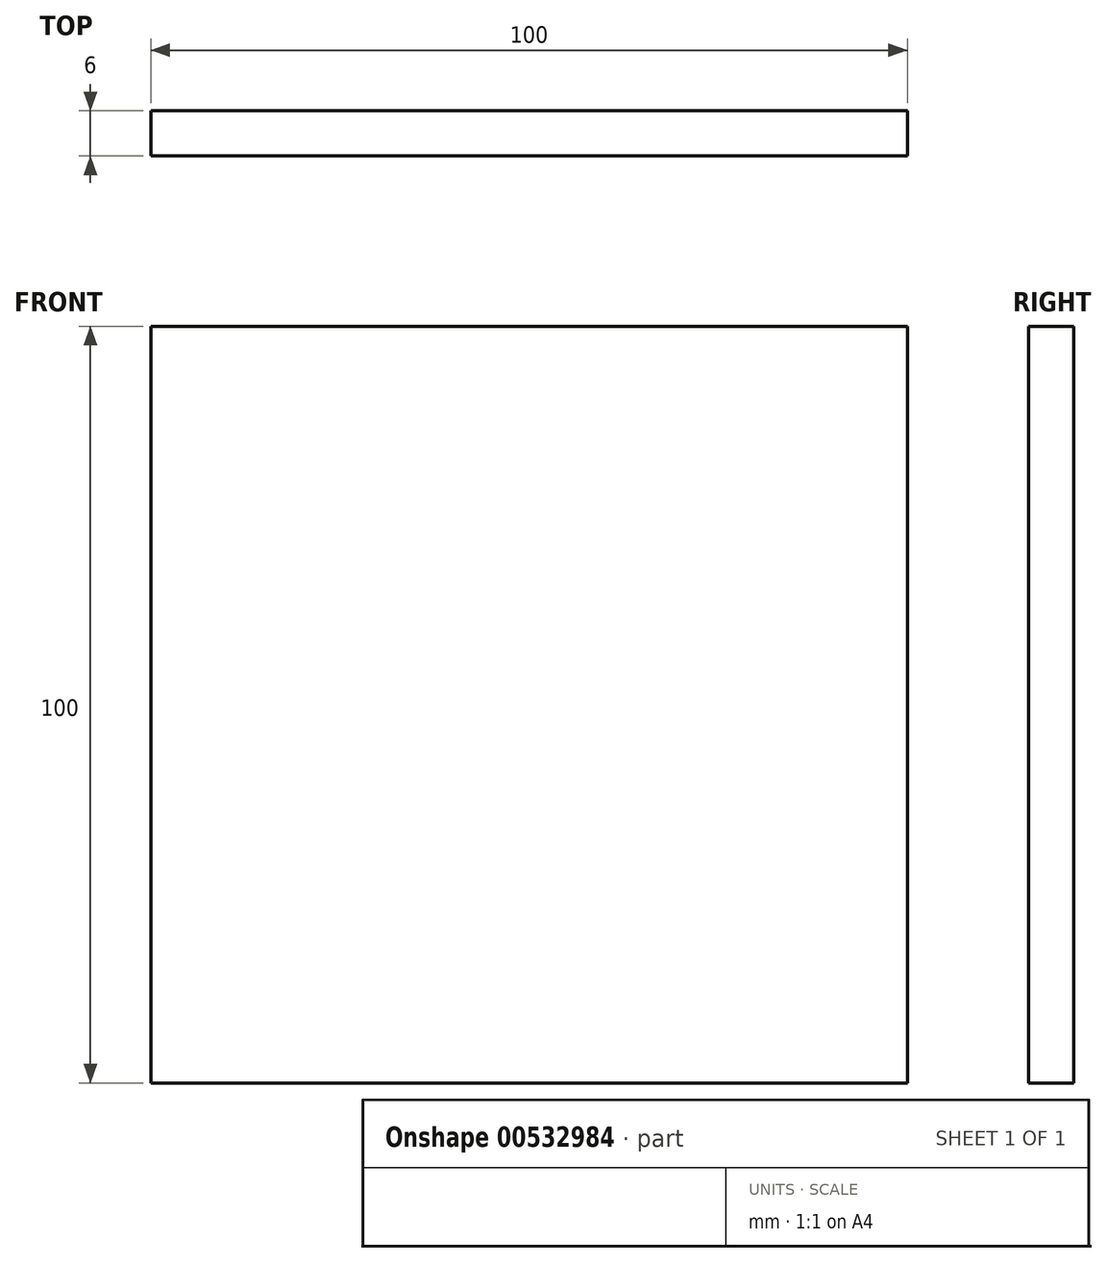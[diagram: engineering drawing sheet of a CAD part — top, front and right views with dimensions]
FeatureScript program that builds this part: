
annotation { "Feature Type Name" : "Feature", "Feature Type Description" : "" }
export const myFeature = defineFeature(function(context is Context, id is Id, definition is map)
    precondition{}
    {
        {
            var Q0;
            Q0=qCreatedBy(makeId("Front.planeOp"),FACE);
            var sketch = newSketch(context, id + "F0", { "sketchPlane" : qUnion([Q0])});
            skLineSegment(sketch, "E0.bottom", {"start": v(-49.73, 63.1) * mm, "end": v(50.27, 63.1) * mm});
            skLineSegment(sketch, "E0.top", {"start": v(-49.73, -36.9) * mm, "end": v(50.27, -36.9) * mm});
            skLineSegment(sketch, "E0.left", {"start": v(-49.73, 63.1) * mm, "end": v(-49.73, -36.9) * mm});
            skLineSegment(sketch, "E0.right", {"start": v(50.27, 63.1) * mm, "end": v(50.27, -36.9) * mm});
            skSolve(sketch);
        }
        {
            var Q0;
            Q0 = qSketchRegion(id + "F0", true);
            extrude(context, id + "F1", {"entities" : qUnion([Q0]), "depth" : 6 * mm, "offsetDistance" : 25 * mm});
        }
    });
